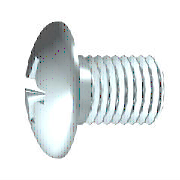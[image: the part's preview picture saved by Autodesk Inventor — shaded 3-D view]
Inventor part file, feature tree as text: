
AUTODESK INVENTOR PART (.ipt)
format: ipt  version: 2013 (Build 170138000, 138)  size: 261,120 bytes
history: native  units: mm (DEFAULTED — no unit token found)
features: sketch x1, plane x1, extrude x1, other x1
ambient origin geometry x7: Origin, YZ Plane, XZ Plane, X Axis, Y Axis, Z Axis, Center Point
bodies: Solid1 (feature_tree), Body (feature_tree)
feature tree (4):
  sketch  "Sketch1"  dims[d1=1.8542mm d2=0.889mm d15=90.0deg d3=-1.3462mm d4=45.0deg d5=0.567267mm d6=1.7018mm d7=0.1778mm d8=3.77031mm d9=0.0mm d12=10.821041mm d13=4.625123mm d16=1.7018mm d17=0.8509mm d52=10.0mm d18=0.872665mm d54=90.0deg d19=0.07112mm d20=0.0mm d21=1.8542mm d22=3.77031mm d23=0.396875mm d24=1.3462mm d25=2.34442mm d27=0.127mm d29=3.6068mm d30=4.7625mm d72=0.0mm d73=0.0mm d74=0.00254mm]
  plane  "Workplane"
  extrude  "Slot"  Depth=0.889mm
  other  "Cut"
